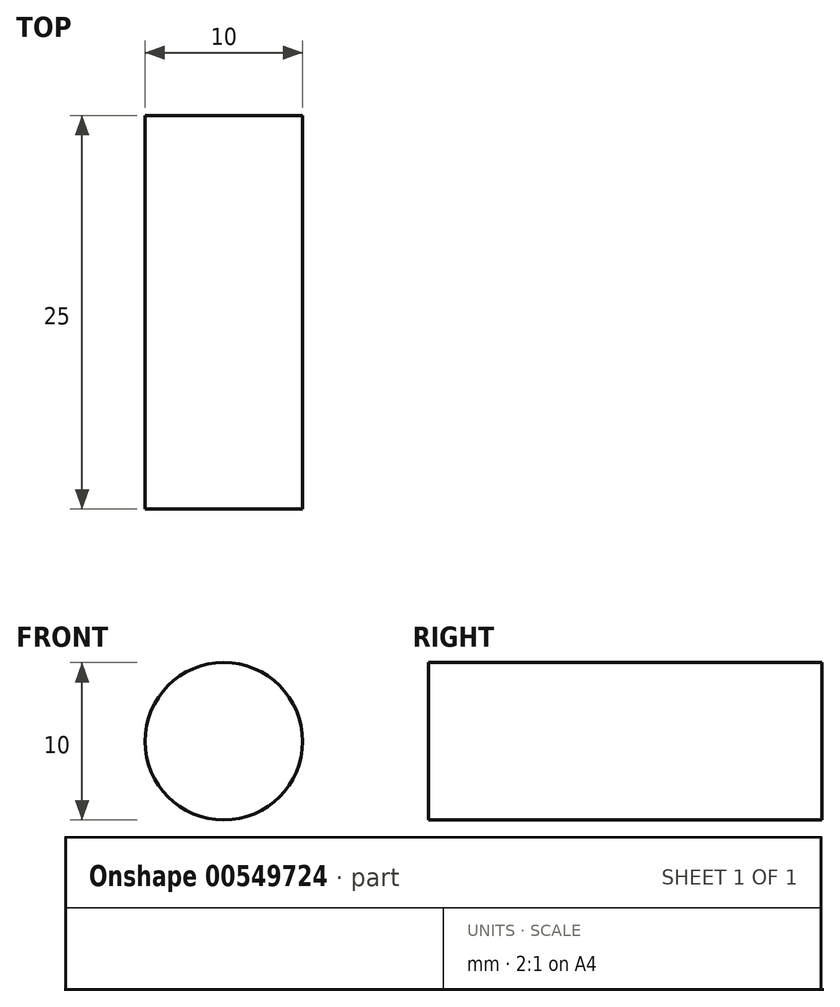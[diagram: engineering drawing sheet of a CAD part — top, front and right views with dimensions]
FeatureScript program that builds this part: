
annotation { "Feature Type Name" : "Feature", "Feature Type Description" : "" }
export const myFeature = defineFeature(function(context is Context, id is Id, definition is map)
    precondition{}
    {
        {
            var Q0;
            Q0=qCreatedBy(makeId("Front.planeOp"),FACE);
            var sketch = newSketch(context, id + "F0", { "sketchPlane" : qUnion([Q0])});
            skCircle(sketch, "E0", {"center": v(0, 0) * mm, "radius": 5 * mm});
            skSolve(sketch);
        }
        {
            var Q0;
            Q0 = qSketchRegion(id + "F0", true);
            extrude(context, id + "F1", {"entities" : qUnion([Q0]), "depth" : 25 * mm, "offsetDistance" : 25 * mm});
        }
    });
